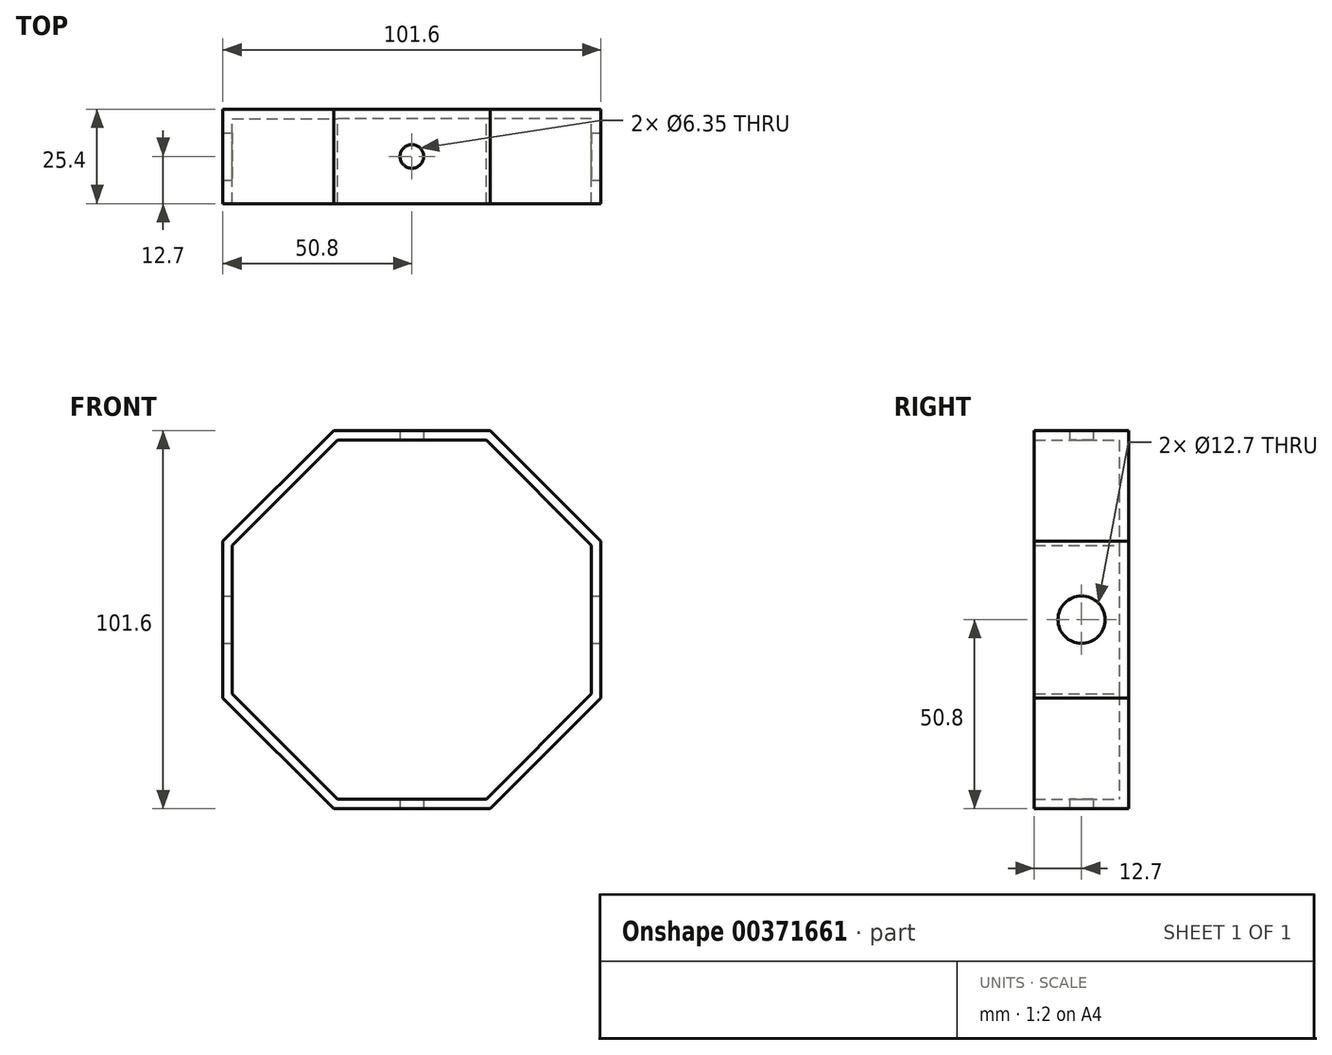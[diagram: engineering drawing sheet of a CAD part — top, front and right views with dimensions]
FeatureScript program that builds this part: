
annotation { "Feature Type Name" : "Feature", "Feature Type Description" : "" }
export const myFeature = defineFeature(function(context is Context, id is Id, definition is map)
    precondition{}
    {
        {
            var Q0;
            Q0=qCreatedBy(makeId("Front.planeOp"),FACE);
            var sketch = newSketch(context, id + "F0", { "sketchPlane" : qUnion([Q0])});
            skLineSegment(sketch, "E0.0", {"start": v(50.8, 21.04) * mm, "end": v(50.8, -21.04) * mm});
            skLineSegment(sketch, "E0.1", {"start": v(50.8, -21.04) * mm, "end": v(21.04, -50.8) * mm});
            skLineSegment(sketch, "E0.2", {"start": v(21.04, -50.8) * mm, "end": v(-21.04, -50.8) * mm});
            skLineSegment(sketch, "E0.3", {"start": v(-21.04, -50.8) * mm, "end": v(-50.8, -21.04) * mm});
            skLineSegment(sketch, "E0.4", {"start": v(-50.8, -21.04) * mm, "end": v(-50.8, 21.04) * mm});
            skLineSegment(sketch, "E0.5", {"start": v(-50.8, 21.04) * mm, "end": v(-21.04, 50.8) * mm});
            skLineSegment(sketch, "E0.6", {"start": v(-21.04, 50.8) * mm, "end": v(21.04, 50.8) * mm});
            skLineSegment(sketch, "E0.7", {"start": v(21.04, 50.8) * mm, "end": v(50.8, 21.04) * mm});
            skPoint(sketch, "E0.0.midPoint", {"position": v(50.8, 0) * mm});
            skFitSpline(sketch, "E1", {"points": [v(-21.04, 50.8) * mm, v(-50.8, 21.04) * mm], "startDerivative": vector(-29.76, -29.76) * mm, "endDerivative": vector(-29.76, -29.76) * mm});
            skLineSegment(sketch, "E2", {"start": v(-21.04, -50.8) * mm, "end": v(-21.04, 50.8) * mm});
            skLineSegment(sketch, "E3", {"start": v(-21.04, -50.8) * mm, "end": v(0, -50.8) * mm});
            skSolve(sketch);
        }
        {
            var Q0;
            Q0 = qSketchRegion(id + "F0", true);
            extrude(context, id + "F1", {"entities" : qUnion([Q0]), "depth" : 25.4 * mm});
        }
        {
            var Q0;
            Q0=makeQuery(id+"F1.opExtrude","CAP_FACE",FACE,{"disambiguationData":[OSD([sQuery(id+"F0.wireOp",EDGE,"E0.0"),sQuery(id+"F0.wireOp",EDGE,"E0.1"),sQuery(id+"F0.wireOp",EDGE,"E0.2"),sQuery(id+"F0.wireOp",EDGE,"E0.3"),sQuery(id+"F0.wireOp",EDGE,"E0.4"),sQuery(id+"F0.wireOp",EDGE,"E0.5"),sQuery(id+"F0.wireOp",EDGE,"E0.6"),sQuery(id+"F0.wireOp",EDGE,"E0.7")])],"isStart":false});
            shell(context, id + "F2", {"entities" : qUnion([Q0]), "thickness" : 2.54 * mm});
        }
        {
            var Q0;
            Q0=makeQuery(id+"F1.opExtrude","SWEPT_FACE",FACE,{"disambiguationData":[OSD([sQuery(id+"F0.wireOp",EDGE,"E0.2")])]});
            var sketch = newSketch(context, id + "F3", { "sketchPlane" : qUnion([Q0])});
            skPoint(sketch, "E4", {"position": v(0, 12.7) * mm});
            skSolve(sketch);
        }
        {
            var Q0;
            Q0=sQuery(id+"F3.wireOp",VERTEX,"E4");
            var Q1;
            Q1=makeQuery(id+"F1.opExtrude","SWEPT_BODY",BODY,{"disambiguationData":[OSD([sQuery(id+"F0.wireOp",EDGE,"E0.0"),sQuery(id+"F0.wireOp",EDGE,"E0.1"),sQuery(id+"F0.wireOp",EDGE,"E0.2"),sQuery(id+"F0.wireOp",EDGE,"E0.3"),sQuery(id+"F0.wireOp",EDGE,"E0.4"),sQuery(id+"F0.wireOp",EDGE,"E0.6"),sQuery(id+"F0.wireOp",EDGE,"E0.7"),sQuery(id+"F0.wireOp",EDGE,"E1")])]});
            hole(context, id + "F4", {"style" : HoleStyle.SIMPLE, "endStyle" : HoleEndStyle.THROUGH, "holeDiameter" : 6.35 * mm, "isTappedThrough" : true, "tappedDepth" : 12.7 * mm, "tapClearance" : 3, "startFromSketch" : true, "locations" : qUnion([Q0]), "scope" : qUnion([Q1])});
        }
        {
            var Q0;
            Q0=makeQuery(id+"F1.opExtrude","SWEPT_FACE",FACE,{"disambiguationData":[OSD([sQuery(id+"F0.wireOp",EDGE,"E0.0")])]});
            var sketch = newSketch(context, id + "F5", { "sketchPlane" : qUnion([Q0])});
            skPoint(sketch, "E5", {"position": v(-12.7, 0) * mm});
            skSolve(sketch);
        }
        {
            var Q0;
            Q0=sQuery(id+"F5.wireOp",VERTEX,"E5");
            var Q1;
            Q1=makeQuery(id+"F1.opExtrude","SWEPT_BODY",BODY,{"disambiguationData":[OSD([sQuery(id+"F0.wireOp",EDGE,"E0.0"),sQuery(id+"F0.wireOp",EDGE,"E0.1"),sQuery(id+"F0.wireOp",EDGE,"E0.2"),sQuery(id+"F0.wireOp",EDGE,"E0.3"),sQuery(id+"F0.wireOp",EDGE,"E0.4"),sQuery(id+"F0.wireOp",EDGE,"E0.6"),sQuery(id+"F0.wireOp",EDGE,"E0.7"),sQuery(id+"F0.wireOp",EDGE,"E1")])]});
            hole(context, id + "F6", {"style" : HoleStyle.SIMPLE, "endStyle" : HoleEndStyle.THROUGH, "holeDiameter" : 12.7 * mm, "isTappedThrough" : true, "tappedDepth" : 12.7 * mm, "tapClearance" : 3, "startFromSketch" : true, "locations" : qUnion([Q0]), "scope" : qUnion([Q1])});
        }
    });
